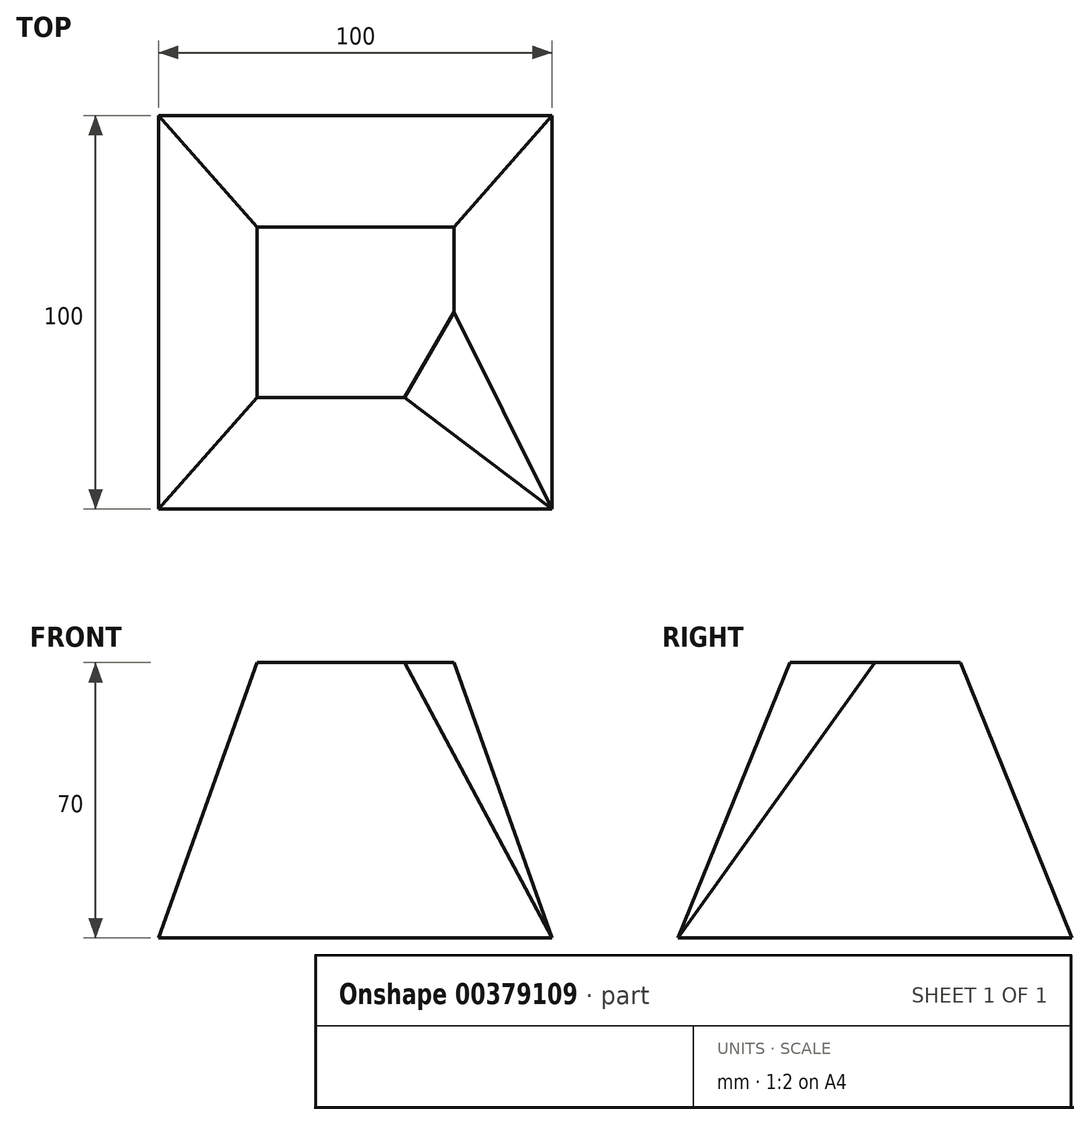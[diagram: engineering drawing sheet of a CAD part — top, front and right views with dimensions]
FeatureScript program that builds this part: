
annotation { "Feature Type Name" : "Feature", "Feature Type Description" : "" }
export const myFeature = defineFeature(function(context is Context, id is Id, definition is map)
    precondition{}
    {
        {
            var Q0;
            Q0=qCreatedBy(makeId("Top.planeOp"),FACE);
            cPlane(context, id + "F0", {"entities" : qUnion([Q0]), "cplaneType" : CPlaneType.OFFSET, "offset" : 70 * mm, "width" : 150 * mm, "height" : 150 * mm});
        }
        {
            var Q0;
            Q0=qCreatedBy(makeId("Top.planeOp"),FACE);
            var sketch = newSketch(context, id + "F1", { "sketchPlane" : qUnion([Q0])});
            skLineSegment(sketch, "E0.bottom", {"start": v(50, -50) * mm, "end": v(-50, -50) * mm});
            skLineSegment(sketch, "E0.top", {"start": v(50, 50) * mm, "end": v(-50, 50) * mm});
            skLineSegment(sketch, "E0.left", {"start": v(50, -50) * mm, "end": v(50, 50) * mm});
            skLineSegment(sketch, "E0.right", {"start": v(-50, -50) * mm, "end": v(-50, 50) * mm});
            skPoint(sketch, "E0.middle", {"position": v(0, 0) * mm});
            skSolve(sketch);
        }
        {
            var Q0;
            Q0=qCreatedBy(id+"F0.planeOp",FACE);
            var sketch = newSketch(context, id + "F2", { "sketchPlane" : qUnion([Q0])});
            skCircle(sketch, "E1.cCircle", {"center": v(0, 0) * mm, "radius": 25 * mm, "construction": true});
            skLineSegment(sketch, "E1.0", {"start": v(25, 0) * mm, "end": v(12.5, -21.65) * mm});
            skLineSegment(sketch, "E1.1", {"start": v(12.5, -21.65) * mm, "end": v(-12.5, -21.65) * mm});
            skLineSegment(sketch, "E1.2", {"start": v(-12.5, -21.65) * mm, "end": v(-25, 0) * mm});
            skLineSegment(sketch, "E1.3", {"start": v(-25, 0) * mm, "end": v(-12.5, 21.65) * mm});
            skLineSegment(sketch, "E1.4", {"start": v(-12.5, 21.65) * mm, "end": v(12.5, 21.65) * mm});
            skLineSegment(sketch, "E1.5", {"start": v(12.5, 21.65) * mm, "end": v(25, 0) * mm});
            skSolve(sketch);
        }
        {
            var Q0;
            Q0=qCreatedBy(id+"F0.planeOp",FACE);
            var sketch = newSketch(context, id + "F3", { "sketchPlane" : qUnion([Q0])});
            skLineSegment(sketch, "E2.0", {"start": v(-12.5, 21.65) * mm, "end": v(12.5, 21.65) * mm, "construction": true});
            skLineSegment(sketch, "E3.0.0", {"start": v(25, 0) * mm, "end": v(12.5, 21.65) * mm, "construction": true});
            skLineSegment(sketch, "E3.0.1", {"start": v(12.5, 21.65) * mm, "end": v(-12.5, 21.65) * mm, "construction": true});
            skLineSegment(sketch, "E3.0.2", {"start": v(-12.5, 21.65) * mm, "end": v(-25, 0) * mm, "construction": true});
            skLineSegment(sketch, "E3.0.3", {"start": v(-25, 0) * mm, "end": v(-12.5, -21.65) * mm, "construction": true});
            skLineSegment(sketch, "E3.0.4", {"start": v(-12.5, -21.65) * mm, "end": v(12.5, -21.65) * mm, "construction": true});
            skLineSegment(sketch, "E3.0.5", {"start": v(12.5, -21.65) * mm, "end": v(25, 0) * mm, "construction": true});
            skLineSegment(sketch, "E4.bottom", {"start": v(25, -21.65) * mm, "end": v(-25, -21.65) * mm});
            skLineSegment(sketch, "E4.top", {"start": v(25, 21.65) * mm, "end": v(-25, 21.65) * mm});
            skLineSegment(sketch, "E4.left", {"start": v(25, -21.65) * mm, "end": v(25, 21.65) * mm});
            skLineSegment(sketch, "E4.right", {"start": v(-25, -21.65) * mm, "end": v(-25, 21.65) * mm});
            skPoint(sketch, "E4.middle", {"position": v(0, 0) * mm});
            skSolve(sketch);
        }
        {
            var Q0;
            Q0=makeQuery(id+"F1.imprint","IMPRINT",FACE,{"disambiguationData":[TD([[makeQuery(id+"F1.imprint","IMPRINT",EDGE,{"derivedFrom":sQuery(id+"F1.wireOp",EDGE,"E0.bottom")}),-1.0]])]});
            var Q1;
            Q1=makeQuery(id+"F3.imprint","IMPRINT",FACE,{"disambiguationData":[TD([[makeQuery(id+"F3.imprint","IMPRINT",EDGE,{"derivedFrom":sQuery(id+"F3.wireOp",EDGE,"E4.bottom")}),-1.0]])]});
            loft(context, id + "F4", {"sheetProfilesArray" : [{ "sheetProfileEntities" : qUnion([Q0]) }, { "sheetProfileEntities" : qUnion([Q1]) }]});
        }
        {
            var Q0;
            Q0=qCreatedBy(id+"F0.planeOp",FACE);
            var sketch = newSketch(context, id + "F5", { "sketchPlane" : qUnion([Q0])});
            skLineSegment(sketch, "E5.0.0", {"start": v(25, 0) * mm, "end": v(12.5, 21.65) * mm, "construction": true});
            skLineSegment(sketch, "E5.0.2", {"start": v(-12.5, 21.65) * mm, "end": v(-25, 0) * mm, "construction": true});
            skLineSegment(sketch, "E5.0.3", {"start": v(-25, 0) * mm, "end": v(-12.5, -21.65) * mm, "construction": true});
            skLineSegment(sketch, "E5.0.5", {"start": v(12.5, -21.65) * mm, "end": v(25, 0) * mm, "construction": true});
            skLineSegment(sketch, "E6", {"start": v(12.5, 21.65) * mm, "end": v(25, 0) * mm});
            skLineSegment(sketch, "E7", {"start": v(25, 21.65) * mm, "end": v(12.5, 21.65) * mm});
            skLineSegment(sketch, "E8", {"start": v(-12.5, 21.65) * mm, "end": v(-25, 0) * mm});
            skLineSegment(sketch, "E9", {"start": v(-25, 21.65) * mm, "end": v(-12.5, 21.65) * mm});
            skLineSegment(sketch, "E10", {"start": v(-12.5, -21.65) * mm, "end": v(-25, 0) * mm});
            skLineSegment(sketch, "E11", {"start": v(25, 0) * mm, "end": v(25, -21.65) * mm});
            skLineSegment(sketch, "E12", {"start": v(12.5, -21.65) * mm, "end": v(25, 0) * mm});
            skLineSegment(sketch, "E13", {"start": v(25, 21.65) * mm, "end": v(25, 0) * mm});
            skLineSegment(sketch, "E14", {"start": v(12.5, -21.65) * mm, "end": v(25, -21.65) * mm});
            skLineSegment(sketch, "E15", {"start": v(-25, 21.65) * mm, "end": v(-25, 0) * mm});
            skLineSegment(sketch, "E16", {"start": v(-25, 0) * mm, "end": v(-25, -21.65) * mm});
            skLineSegment(sketch, "E17", {"start": v(-25, -21.65) * mm, "end": v(-12.5, -21.65) * mm});
            skSolve(sketch);
        }
        {
            var Q1;
            Q1=makeQuery(id+"F5.imprint","IMPRINT",FACE,{"disambiguationData":[TD([[makeQuery(id+"F5.imprint","IMPRINT",EDGE,{"derivedFrom":sQuery(id+"F5.wireOp",EDGE,"E11")}),-1.0]])]});
            var Q2;
            Q2=sQuery(id+"F1.wireOp",VERTEX,"E0.left.start");
            loft(context, id + "F6", {"operationType" : NewBodyOperationType.REMOVE, "sheetProfilesArray" : [{ "sheetProfileEntities" : qUnion([Q1]) }, { "sheetProfileEntities" : qUnion([Q2]) }]});
        }
    });
